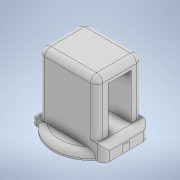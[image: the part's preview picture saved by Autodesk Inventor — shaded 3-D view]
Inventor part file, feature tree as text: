
AUTODESK INVENTOR PART (.ipt)
format: ipt  version: 2020 (Build 240168000, 168)  size: 233,984 bytes
history: native  units: in
note: dims shown in document units (in); Inventor stores cm internally (conversion verified against a paired STEP export)
features: extrude x5, sketch x5, direct_edit x1, fillet x1, move_body x1
ambient origin geometry x8: Origin, YZ Plane, XZ Plane, XY Plane, X Axis, Y Axis, Z Axis, Center Point
bodies: Solid1 (feature_tree)
feature tree (13):
  extrude  "Extrusion1"  Depth=1.0in
  extrude  "Extrusion2"  Depth=0.0591in
  extrude  "Extrusion3"  Depth=0.0787in TaperAngle=0.0deg
  extrude  "Extrusion4"  Depth=0.1693in
  direct_edit  "Direct Edit1"
  extrude  "Extrusion5"  Depth=0.125in
  fillet  "Fillet1"  Radius=0.1693in
  sketch  "Sketch1"  dims[d0=1.5in d1=1.0in]
  sketch  "Sketch2"  dims[d2=0.315in d3=0.0591in]
  sketch  "Sketch3"  dims[d4=1.5748in d6=360.0deg d8=0.0787in d9=0.0in]
  sketch  "Sketch4"  dims[d10=0.0787in d11=0.0in d12=0.1693in]
  sketch  "Sketch5"  dims[d13=0.4724in d14=0.4724in d15=0.1693in d16=0.315in d17=0.0in d18=0.9449in d19=0.2362in d20=0.2362in d21=0.1693in d22=0.0in d23=0.0in d24=0.0in d25=1.188in d26=0.1693in d27=0.0in d28=0.125in d29=0.0344in]
  move_body  "Move1"
